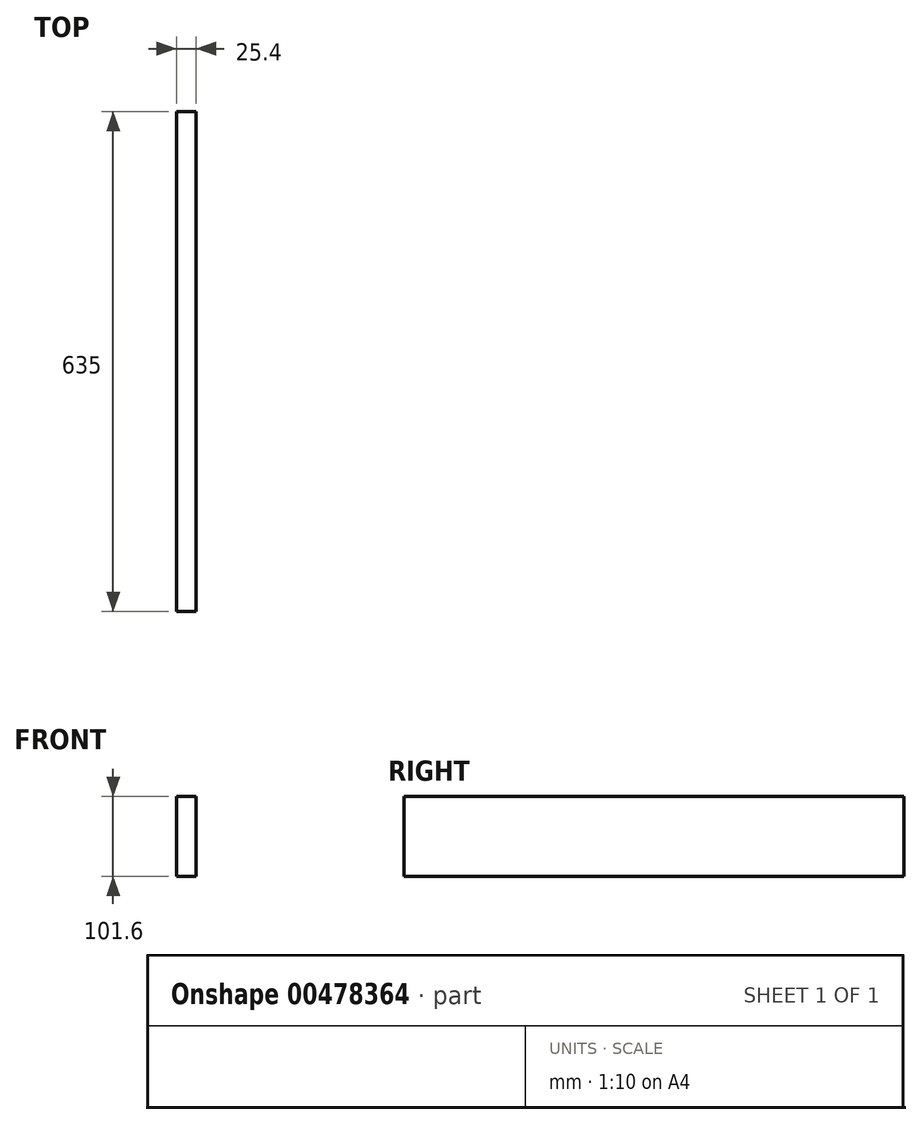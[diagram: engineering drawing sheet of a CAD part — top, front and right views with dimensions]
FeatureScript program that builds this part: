
annotation { "Feature Type Name" : "Feature", "Feature Type Description" : "" }
export const myFeature = defineFeature(function(context is Context, id is Id, definition is map)
    precondition{}
    {
        {
            var Q0;
            Q0=qCreatedBy(makeId("Right.planeOp"),FACE);
            var sketch = newSketch(context, id + "F0", { "sketchPlane" : qUnion([Q0])});
            skLineSegment(sketch, "E0.bottom", {"start": v(-373.67, 84.18) * mm, "end": v(261.33, 84.18) * mm});
            skLineSegment(sketch, "E0.top", {"start": v(-373.67, -17.42) * mm, "end": v(261.33, -17.42) * mm});
            skLineSegment(sketch, "E0.left", {"start": v(-373.67, 84.18) * mm, "end": v(-373.67, -17.42) * mm});
            skLineSegment(sketch, "E0.right", {"start": v(261.33, 84.18) * mm, "end": v(261.33, -17.42) * mm});
            skSolve(sketch);
        }
        {
            var Q0;
            Q0 = qSketchRegion(id + "F0", true);
            extrude(context, id + "F1", {"entities" : qUnion([Q0]), "depth" : 25.4 * mm, "offsetDistance" : 25.4 * mm});
        }
    });
